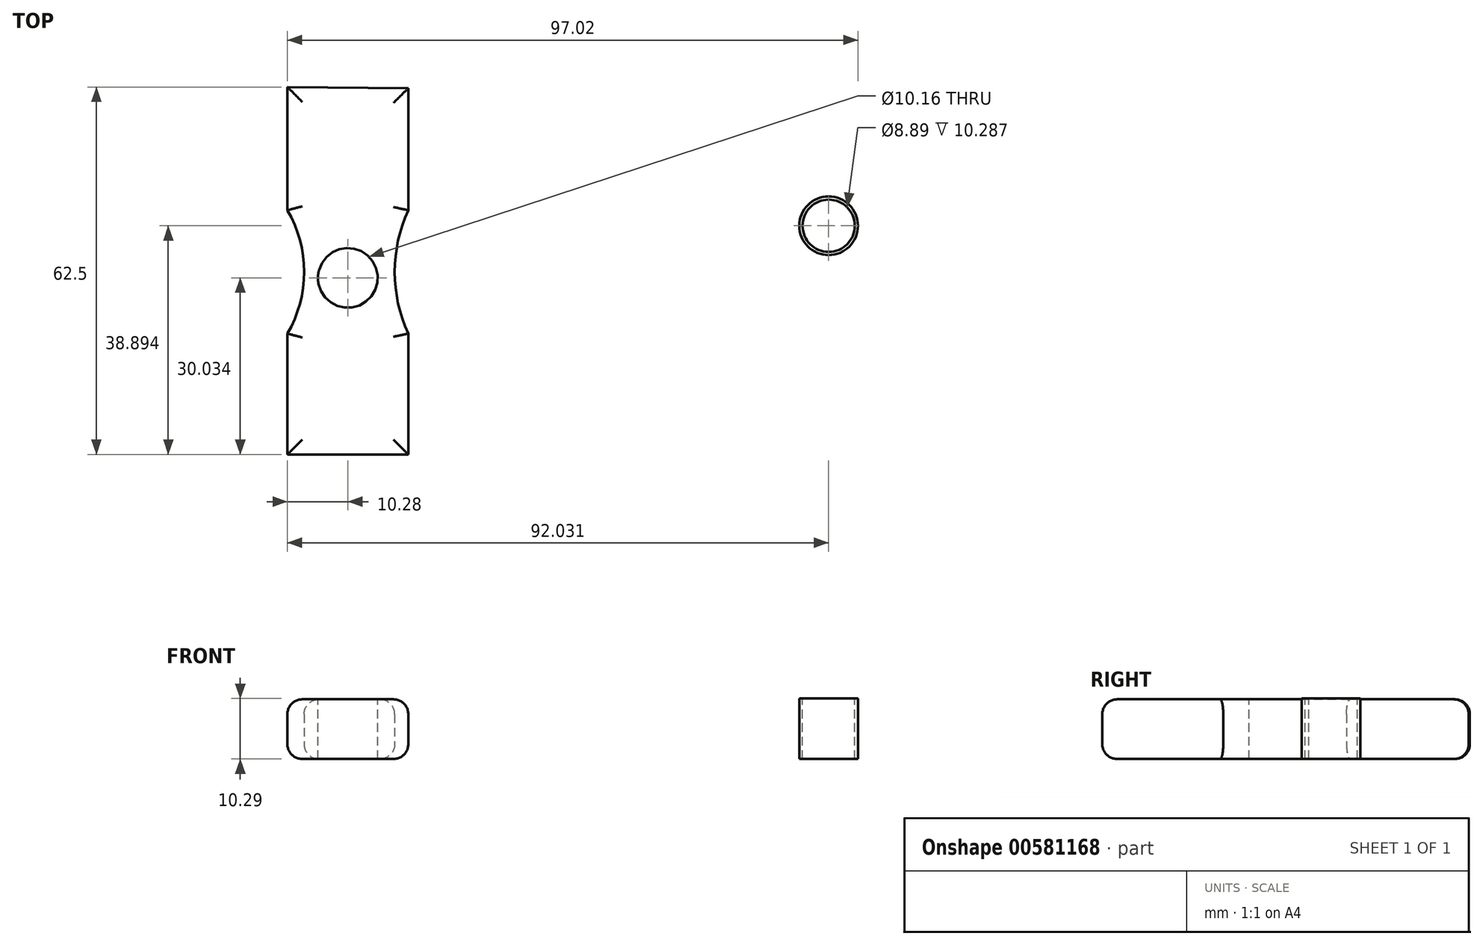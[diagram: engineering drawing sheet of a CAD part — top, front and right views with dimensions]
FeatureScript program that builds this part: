
annotation { "Feature Type Name" : "Feature", "Feature Type Description" : "" }
export const myFeature = defineFeature(function(context is Context, id is Id, definition is map)
    precondition{}
    {
        {
            var Q0;
            Q0=qCreatedBy(makeId("Top.planeOp"),FACE);
            var sketch = newSketch(context, id + "F0", { "sketchPlane" : qUnion([Q0])});
            skLineSegment(sketch, "E0", {"start": v(-57.97, 27.13) * mm, "end": v(-57.97, 6.16) * mm});
            skLineSegment(sketch, "E1", {"start": v(-57.97, -14.81) * mm, "end": v(-57.97, -35.37) * mm});
            skLineSegment(sketch, "E2", {"start": v(-37.4, -14.81) * mm, "end": v(-37.4, -35.37) * mm});
            skLineSegment(sketch, "E3", {"start": v(-37.4, 6.16) * mm, "end": v(-37.4, 26.92) * mm});
            skLineSegment(sketch, "E4", {"start": v(-57.97, 27.13) * mm, "end": v(-37.4, 26.92) * mm});
            skLineSegment(sketch, "E5", {"start": v(-57.97, -35.37) * mm, "end": v(-37.4, -35.37) * mm});
            skArc(sketch, "E6", {"start": v(-57.97, -14.81) * mm, "mid": v(-55.13, -4.33) * mm, "end": v(-57.97, 6.16) * mm});
            skArc(sketch, "E7", {"start": v(-37.4, 6.16) * mm, "mid": v(-39.72, -4.33) * mm, "end": v(-37.4, -14.81) * mm});
            skArc(sketch, "E8", {"start": v(-8.1, -10.33) * mm, "mid": v(33.74, -8.1) * mm, "end": v(-5.65, 6.16) * mm});
            skSolve(sketch);
        }
        {
            var Q0;
            Q0=makeQuery(id+"F0.imprint","IMPRINT",FACE,{"disambiguationData":[TD([[makeQuery(id+"F0.imprint","IMPRINT",EDGE,{"derivedFrom":sQuery(id+"F0.wireOp",EDGE,"E0")}),1.0]])]});
            extrude(context, id + "F1", {"entities" : qUnion([Q0]), "depth" : 10.16 * mm, "offsetDistance" : 25.4 * mm});
        }
        {
            var Q0;
            Q0=makeQuery(id+"F1.opExtrude","CAP_FACE",FACE,{"disambiguationData":[OSD([sQuery(id+"F0.wireOp",EDGE,"E0"),sQuery(id+"F0.wireOp",EDGE,"E1"),sQuery(id+"F0.wireOp",EDGE,"E2"),sQuery(id+"F0.wireOp",EDGE,"E3"),sQuery(id+"F0.wireOp",EDGE,"E4"),sQuery(id+"F0.wireOp",EDGE,"E5"),sQuery(id+"F0.wireOp",EDGE,"E6"),sQuery(id+"F0.wireOp",EDGE,"E7")])],"isStart":false});
            fillet(context, id + "F2", {"entities" : qUnion([Q0]), "radius" : 2.54 * mm, "tangentPropagation" : true, "allowEdgeOverflow" : false});
        }
        {
            var Q0;
            Q0=makeQuery(id+"F1.opExtrude","CAP_FACE",FACE,{"disambiguationData":[OSD([sQuery(id+"F0.wireOp",EDGE,"E0"),sQuery(id+"F0.wireOp",EDGE,"E1"),sQuery(id+"F0.wireOp",EDGE,"E2"),sQuery(id+"F0.wireOp",EDGE,"E3"),sQuery(id+"F0.wireOp",EDGE,"E4"),sQuery(id+"F0.wireOp",EDGE,"E5"),sQuery(id+"F0.wireOp",EDGE,"E6"),sQuery(id+"F0.wireOp",EDGE,"E7")])],"isStart":true});
            fillet(context, id + "F3", {"entities" : qUnion([Q0]), "radius" : 2.54 * mm, "tangentPropagation" : true, "allowEdgeOverflow" : false});
        }
        {
            var Q0;
            Q0=makeQuery(id+"F1.opExtrude","CAP_FACE",FACE,{"disambiguationData":[OSD([sQuery(id+"F0.wireOp",EDGE,"E0"),sQuery(id+"F0.wireOp",EDGE,"E1"),sQuery(id+"F0.wireOp",EDGE,"E2"),sQuery(id+"F0.wireOp",EDGE,"E3"),sQuery(id+"F0.wireOp",EDGE,"E4"),sQuery(id+"F0.wireOp",EDGE,"E5"),sQuery(id+"F0.wireOp",EDGE,"E6"),sQuery(id+"F0.wireOp",EDGE,"E7")])],"isStart":false});
            var sketch = newSketch(context, id + "F4", { "sketchPlane" : qUnion([Q0])});
            skPoint(sketch, "E9", {"position": v(-47.7, -5.34) * mm});
            skPoint(sketch, "E9.positionSnap0", {"position": v(-47.7, -32.83) * mm});
            skSolve(sketch);
        }
        {
            var Q0;
            Q0=sQuery(id+"F4.wireOp",VERTEX,"E9");
            var Q1;
            Q1=makeQuery(id+"F1.opExtrude","SWEPT_BODY",BODY,{"disambiguationData":[OSD([sQuery(id+"F0.wireOp",EDGE,"E0"),sQuery(id+"F0.wireOp",EDGE,"E1"),sQuery(id+"F0.wireOp",EDGE,"E2"),sQuery(id+"F0.wireOp",EDGE,"E3"),sQuery(id+"F0.wireOp",EDGE,"E4"),sQuery(id+"F0.wireOp",EDGE,"E5"),sQuery(id+"F0.wireOp",EDGE,"E6"),sQuery(id+"F0.wireOp",EDGE,"E7")])]});
            hole(context, id + "F5", {"style" : HoleStyle.SIMPLE, "endStyle" : HoleEndStyle.BLIND, "holeDiameter" : 10.16 * mm, "majorDiameter" : 6.35 * mm, "holeDepth" : 12.7 * mm, "isTappedThrough" : true, "tappedDepth" : 12.7 * mm, "tapClearance" : 3, "locations" : qUnion([Q0]), "scope" : qUnion([Q1])});
        }
        {
            var Q0;
            Q0=qCreatedBy(makeId("Top.planeOp"),FACE);
            var sketch = newSketch(context, id + "F6", { "sketchPlane" : qUnion([Q0])});
            skCircle(sketch, "E10", {"center": v(34.06, 3.52) * mm, "radius": 4.99 * mm});
            skSolve(sketch);
        }
        {
            var Q0;
            Q0=makeQuery(id+"F6.imprint","IMPRINT",FACE,{"disambiguationData":[TD([[makeQuery(id+"F6.imprint","IMPRINT",EDGE,{"derivedFrom":sQuery(id+"F6.wireOp",EDGE,"E10")}),1.0]])]});
            extrude(context, id + "F7", {"entities" : qUnion([Q0]), "depth" : 10.29 * mm, "offsetDistance" : 25.4 * mm});
        }
        {
            var Q0;
            Q0=makeQuery(id+"F7.opExtrude","CAP_FACE",FACE,{"disambiguationData":[OSD([sQuery(id+"F6.wireOp",EDGE,"E10")])],"isStart":false});
            var sketch = newSketch(context, id + "F8", { "sketchPlane" : qUnion([Q0])});
            skPoint(sketch, "E11", {"position": v(34.06, 3.52) * mm});
            skSolve(sketch);
        }
        {
            var Q0;
            Q0=sQuery(id+"F8.wireOp",VERTEX,"E11");
            var Q1;
            Q1=makeQuery(id+"F7.opExtrude","SWEPT_BODY",BODY,{"disambiguationData":[OSD([sQuery(id+"F6.wireOp",EDGE,"E10")])]});
            hole(context, id + "F9", {"style" : HoleStyle.SIMPLE, "endStyle" : HoleEndStyle.THROUGH, "holeDiameter" : 8.9 * mm, "majorDiameter" : 6.35 * mm, "isTappedThrough" : true, "tappedDepth" : 12.7 * mm, "tapClearance" : 3, "locations" : qUnion([Q0]), "scope" : qUnion([Q1])});
        }
    });
